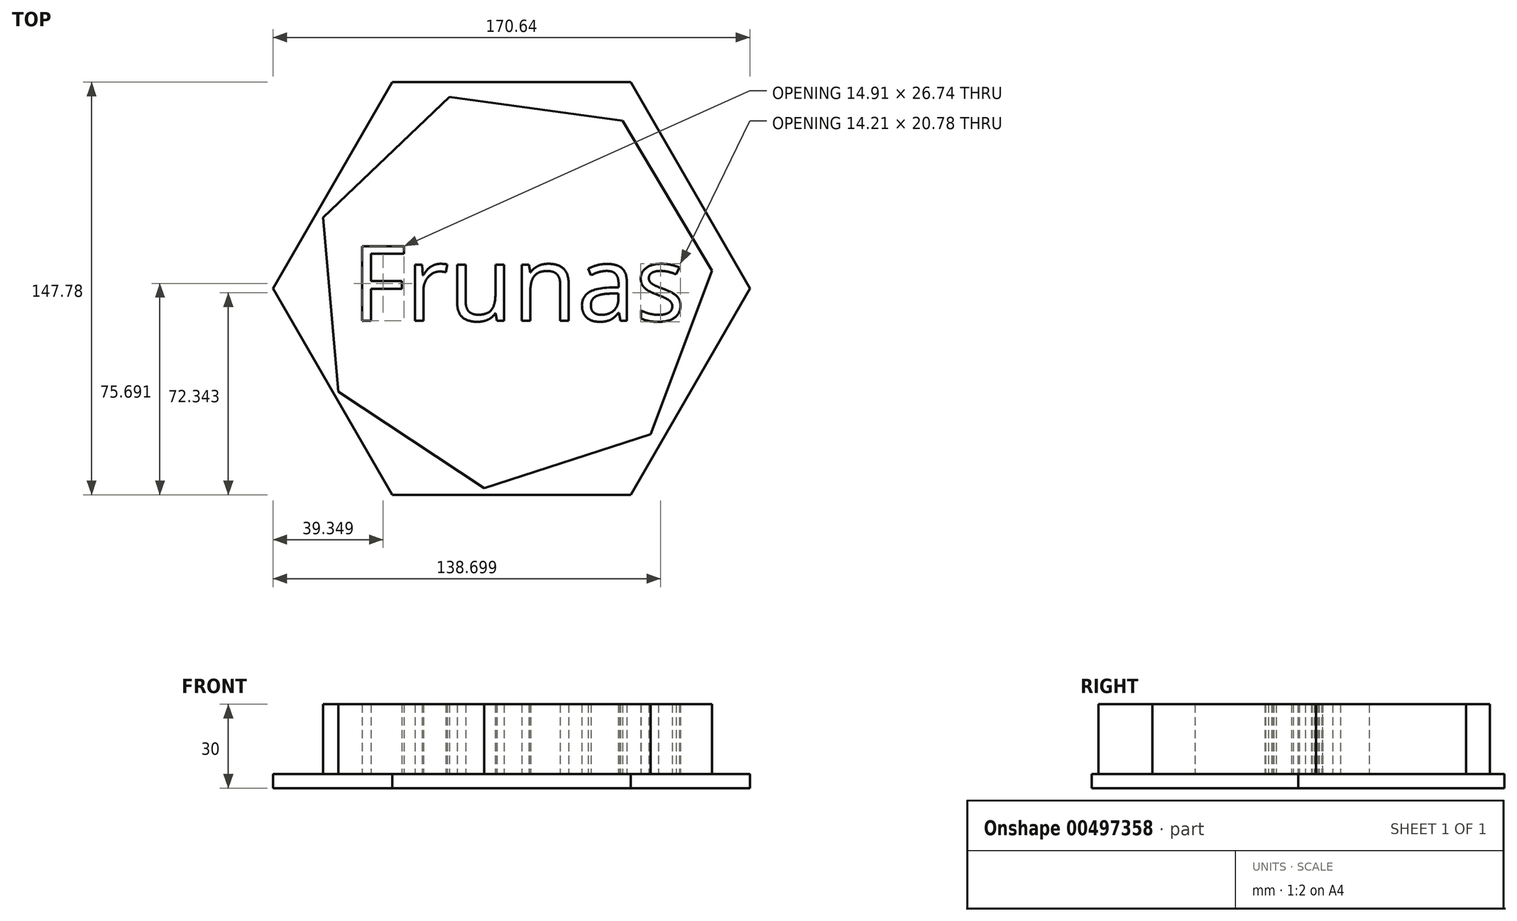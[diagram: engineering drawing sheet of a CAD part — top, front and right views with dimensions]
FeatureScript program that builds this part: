
annotation { "Feature Type Name" : "Feature", "Feature Type Description" : "" }
export const myFeature = defineFeature(function(context is Context, id is Id, definition is map)
    precondition{}
    {
        {
            var Q0;
            Q0=qCreatedBy(makeId("Top.planeOp"),FACE);
            var sketch = newSketch(context, id + "F0", { "sketchPlane" : qUnion([Q0])});
            skCircle(sketch, "E0.cCircle", {"center": v(0, 0) * mm, "radius": 64.97 * mm, "construction": true});
            skLineSegment(sketch, "E0.0", {"start": v(-9.78, -71.44) * mm, "end": v(-61.95, -36.9) * mm});
            skLineSegment(sketch, "E0.1", {"start": v(-61.95, -36.9) * mm, "end": v(-67.47, 25.43) * mm});
            skLineSegment(sketch, "E0.2", {"start": v(-67.47, 25.43) * mm, "end": v(-22.18, 68.61) * mm});
            skLineSegment(sketch, "E0.3", {"start": v(-22.18, 68.61) * mm, "end": v(39.81, 60.12) * mm});
            skLineSegment(sketch, "E0.4", {"start": v(39.81, 60.12) * mm, "end": v(71.83, 6.36) * mm});
            skLineSegment(sketch, "E0.5", {"start": v(71.83, 6.36) * mm, "end": v(49.76, -52.2) * mm});
            skLineSegment(sketch, "E0.6", {"start": v(49.76, -52.2) * mm, "end": v(-9.78, -71.44) * mm});
            skPoint(sketch, "E0.0.midPoint", {"position": v(-35.87, -54.17) * mm});
            skSolve(sketch);
        }
        {
            var Q0;
            Q0=makeQuery(id+"F0.imprint","IMPRINT",FACE,{"disambiguationData":[TD([[makeQuery(id+"F0.imprint","IMPRINT",EDGE,{"derivedFrom":sQuery(id+"F0.wireOp",EDGE,"E0.0")}),-1.0]])]});
            extrude(context, id + "F1", {"entities" : qUnion([Q0]), "depth" : 25 * mm});
        }
        {
            var Q0;
            Q0=qCreatedBy(makeId("Top.planeOp"),FACE);
            var sketch = newSketch(context, id + "F2", { "sketchPlane" : qUnion([Q0])});
            skText(sketch, "E1", { "text": "Frunas", "fontName": "OpenSans-Regular.ttf"});
            const initialGuessF2  = {"E1": [-0.0571, -0.01157, 1, 0, 0.02697]};
            skSetInitialGuess(sketch, initialGuessF2);
            skSolve(sketch);
        }
        {
            var Q0;
            Q0 = qSketchRegion(id + "F2", true);
            extrude(context, id + "F3", {"entities" : qUnion([Q0]), "operationType" : NewBodyOperationType.REMOVE, "depth" : 25 * mm});
        }
        {
            var Q0;
            Q0=qCreatedBy(makeId("Top.planeOp"),FACE);
            var sketch = newSketch(context, id + "F4", { "sketchPlane" : qUnion([Q0])});
            skCircle(sketch, "E2.cCircle", {"center": v(0, 0) * mm, "radius": 73.9 * mm, "construction": true});
            skLineSegment(sketch, "E2.0", {"start": v(-42.66, 73.9) * mm, "end": v(42.66, 73.9) * mm});
            skLineSegment(sketch, "E2.1", {"start": v(42.66, 73.9) * mm, "end": v(85.32, 0) * mm});
            skLineSegment(sketch, "E2.2", {"start": v(85.32, 0) * mm, "end": v(42.66, -73.9) * mm});
            skLineSegment(sketch, "E2.3", {"start": v(42.66, -73.9) * mm, "end": v(-42.66, -73.9) * mm});
            skLineSegment(sketch, "E2.4", {"start": v(-42.66, -73.9) * mm, "end": v(-85.32, 0) * mm});
            skLineSegment(sketch, "E2.5", {"start": v(-85.32, 0) * mm, "end": v(-42.66, 73.9) * mm});
            skPoint(sketch, "E2.0.midPoint", {"position": v(0, 73.9) * mm});
            skSolve(sketch);
        }
        {
            var Q0;
            Q0 = qSketchRegion(id + "F4", true);
            extrude(context, id + "F5", {"entities" : qUnion([Q0]), "oppositeDirection" : true, "depth" : 5 * mm});
        }
    });
